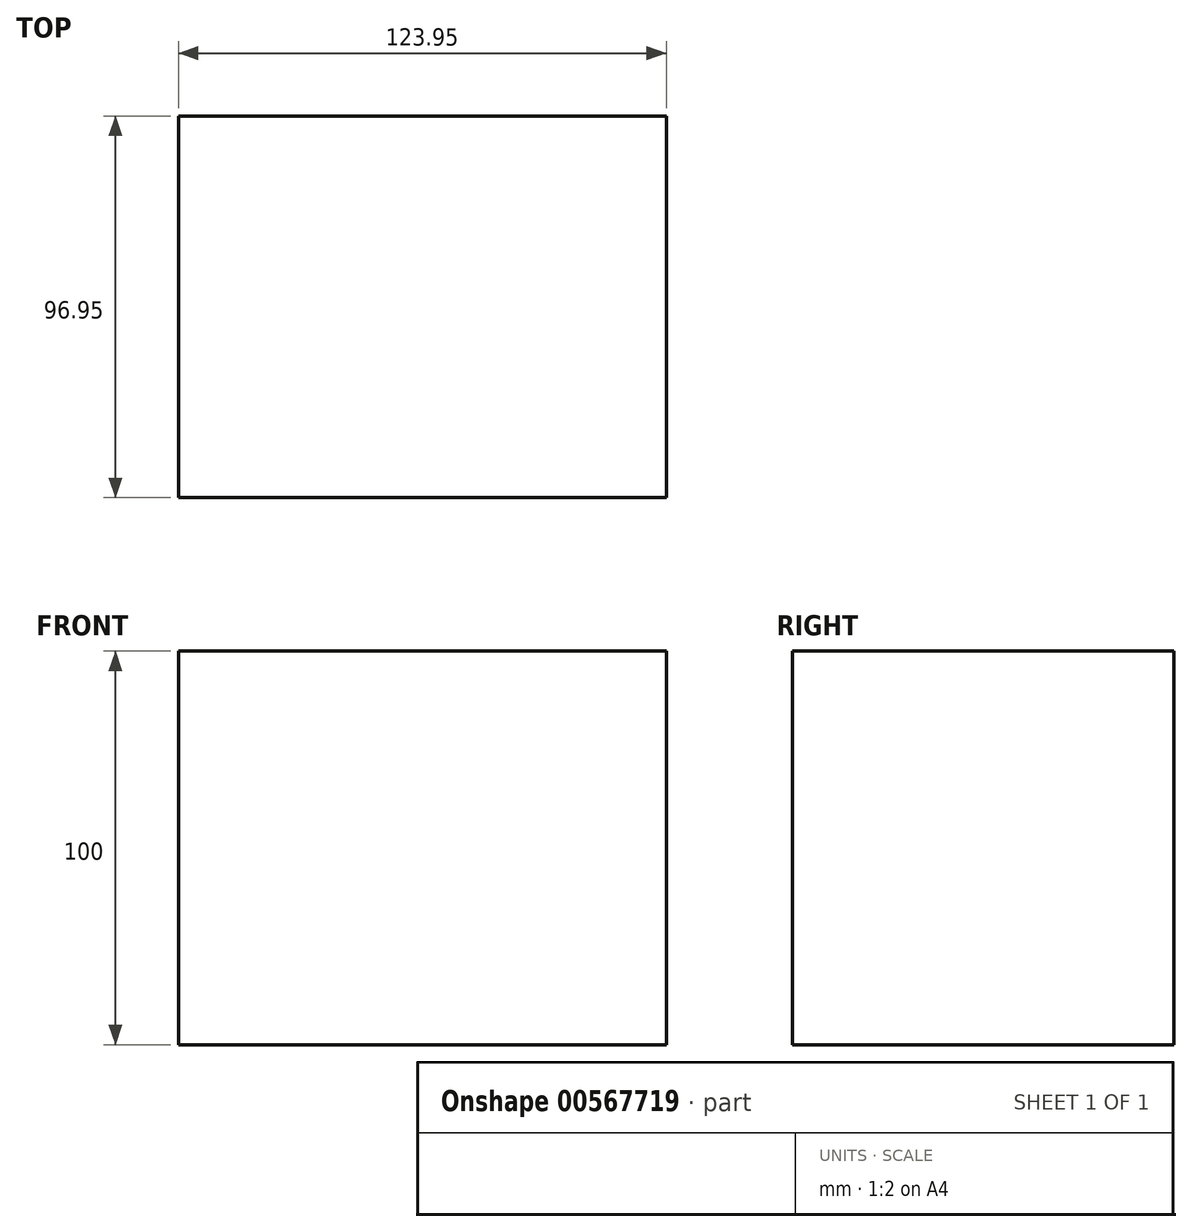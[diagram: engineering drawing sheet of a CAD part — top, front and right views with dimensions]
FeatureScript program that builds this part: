
annotation { "Feature Type Name" : "Feature", "Feature Type Description" : "" }
export const myFeature = defineFeature(function(context is Context, id is Id, definition is map)
    precondition{}
    {
        {
            var Q0;
            Q0=qCreatedBy(makeId("Top.planeOp"),FACE);
            var sketch = newSketch(context, id + "F0", { "sketchPlane" : qUnion([Q0])});
            skLineSegment(sketch, "E0.bottom", {"start": v(-64.43, 47.25) * mm, "end": v(59.52, 47.25) * mm});
            skLineSegment(sketch, "E0.top", {"start": v(-64.43, -49.7) * mm, "end": v(59.52, -49.7) * mm});
            skLineSegment(sketch, "E0.left", {"start": v(-64.43, 47.25) * mm, "end": v(-64.43, -49.7) * mm});
            skLineSegment(sketch, "E0.right", {"start": v(59.52, 47.25) * mm, "end": v(59.52, -49.7) * mm});
            skSolve(sketch);
        }
        {
            var Q0;
            Q0=makeQuery(id+"F0.imprint","IMPRINT",FACE,{"disambiguationData":[TD([[makeQuery(id+"F0.imprint","IMPRINT",EDGE,{"derivedFrom":sQuery(id+"F0.wireOp",EDGE,"E0.bottom")}),-1.0]])]});
            extrude(context, id + "F1", {"entities" : qUnion([Q0]), "depth" : 100 * mm, "offsetDistance" : 25 * mm});
        }
    });
